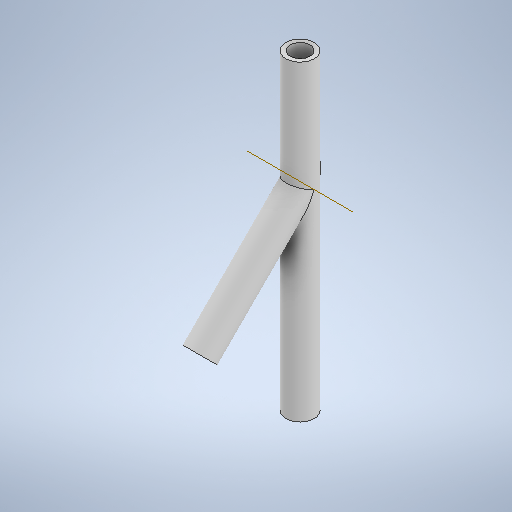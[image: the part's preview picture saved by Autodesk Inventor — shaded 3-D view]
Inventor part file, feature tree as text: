
AUTODESK INVENTOR PART (.ipt)
format: ipt  version: 2025 (Build 290162000, 162)  size: 284,160 bytes
history: native  units: mm
features: extrude x5, sketch x5, other x2
ambient origin geometry x8: Origin, YZ Plane, XZ Plane, XY Plane, X Axis, Y Axis, Z Axis, Center Point
bodies: Body1 (feature_tree)
feature tree (12):
  other  "Bryła1"
  other  "Płaszczyzna konstrukcyjna9"
  extrude  "Wyciągnięcie proste1"  Depth=10.0mm
  extrude  "Wyciągnięcie proste2"  Depth=50.0mm TaperAngle=0.0deg
  extrude  "Wyciągnięcie proste3"  Depth=10.0mm
  extrude  "Wyciągnięcie proste4"  Depth=140.0mm TaperAngle=0.0deg
  extrude  "Wyciągnięcie proste5"  Depth=7.0mm
  sketch  "Szkic5"
  sketch  "Szkic6"
  sketch  "Szkic8"
  sketch  "Szkic9"
  sketch  "Szkic10"
